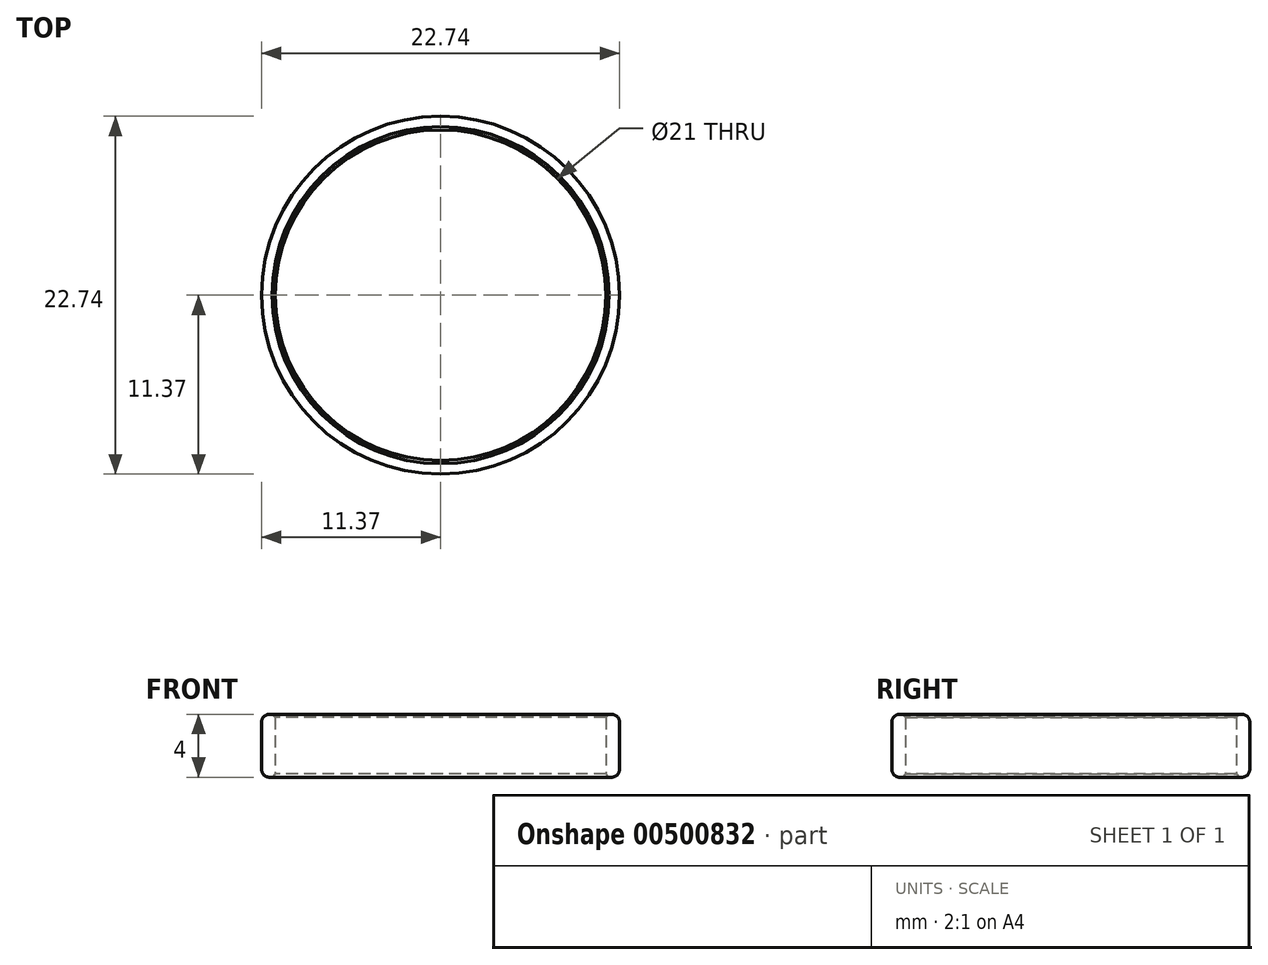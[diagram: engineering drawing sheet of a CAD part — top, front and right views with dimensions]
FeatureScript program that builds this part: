
annotation { "Feature Type Name" : "Feature", "Feature Type Description" : "" }
export const myFeature = defineFeature(function(context is Context, id is Id, definition is map)
    precondition{}
    {
        {
            var Q0;
            Q0=qCreatedBy(makeId("Top.planeOp"),FACE);
            var sketch = newSketch(context, id + "F0", { "sketchPlane" : qUnion([Q0])});
            skCircle(sketch, "E0", {"center": v(0, 0) * mm, "radius": 10.5 * mm});
            skCircle(sketch, "E1", {"center": v(0, 0) * mm, "radius": 11.37 * mm});
            skSolve(sketch);
        }
        {
            var Q0;
            Q0=makeQuery(id+"F0.imprint","IMPRINT",FACE,{"disambiguationData":[TD([[makeQuery(id+"F0.imprint","IMPRINT",EDGE,{"derivedFrom":sQuery(id+"F0.wireOp",EDGE,"E0")}),-1.0]])]});
            extrude(context, id + "F1", {"entities" : qUnion([Q0]), "depth" : 4 * mm});
        }
        {
            var Q0;
            Q0=makeQuery(id+"F1.opExtrude","CAP_EDGE",EDGE,{"disambiguationData":[OSD([sQuery(id+"F0.wireOp",EDGE,"E1")])],"isStart":true});
            var Q1;
            Q1=makeQuery(id+"F1.opExtrude","CAP_EDGE",EDGE,{"disambiguationData":[OSD([sQuery(id+"F0.wireOp",EDGE,"E1")])],"isStart":false});
            fillet(context, id + "F2", {"entities" : qUnion([Q0, Q1]), "radius" : 0.5 * mm, "tangentPropagation" : true, "allowEdgeOverflow" : false});
        }
        {
            var Q0;
            Q0=makeQuery(id+"F1.opExtrude","CAP_EDGE",EDGE,{"disambiguationData":[OSD([sQuery(id+"F0.wireOp",EDGE,"E0")])],"isStart":true});
            var Q1;
            Q1=makeQuery(id+"F1.opExtrude","CAP_EDGE",EDGE,{"disambiguationData":[OSD([sQuery(id+"F0.wireOp",EDGE,"E0")])],"isStart":false});
            chamfer(context, id + "F3", {"entities" : qUnion([Q0, Q1]), "width" : 0.2 * mm, "tangentPropagation" : true});
        }
    });
